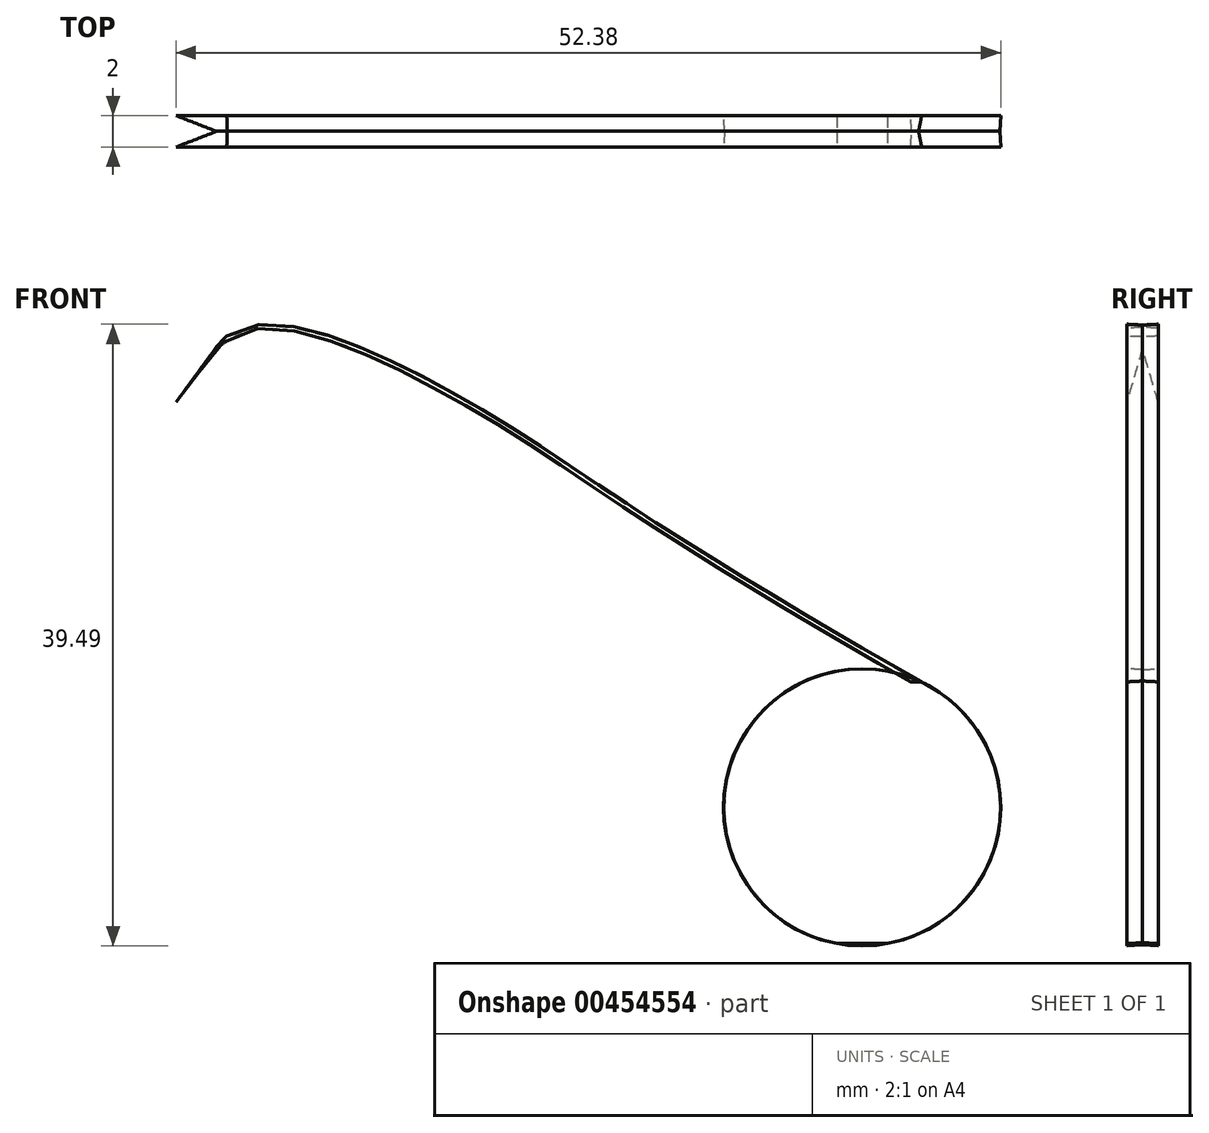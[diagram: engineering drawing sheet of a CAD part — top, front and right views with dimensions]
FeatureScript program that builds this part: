
annotation { "Feature Type Name" : "Feature", "Feature Type Description" : "" }
export const myFeature = defineFeature(function(context is Context, id is Id, definition is map)
    precondition{}
    {
        {
            var Q0;
            Q0=qCreatedBy(makeId("Front.planeOp"),FACE);
            var sketch = newSketch(context, id + "F0", { "sketchPlane" : qUnion([Q0])});
            skCircle(sketch, "E0", {"center": v(-75.56, 14) * mm, "radius": 2 * mm});
            skCircle(sketch, "E1", {"center": v(69.2, 8.6) * mm, "radius": 8.75 * mm});
            skLineSegment(sketch, "E2", {"start": v(-75.56, 14) * mm, "end": v(-75.56, -5.67) * mm});
            skLineSegment(sketch, "E3", {"start": v(-75.56, -5.67) * mm, "end": v(-75.56, 4.17) * mm, "construction": true});
            skSolve(sketch);
        }
        {
            var Q0;
            Q0=makeQuery(id+"F0.imprint","IMPRINT",FACE,{"disambiguationData":[TD([[makeQuery(id+"F0.imprint","IMPRINT",EDGE,{"derivedFrom":sQuery(id+"F0.wireOp",EDGE,"E1")}),1.0]])]});
            var sketch = newSketch(context, id + "F1", { "sketchPlane" : qUnion([Q0])});
            skLineSegment(sketch, "E4", {"start": v(-69.34, 0) * mm, "end": v(75.66, 0) * mm});
            skPoint(sketch, "E5", {"position": v(-60.14, 0) * mm});
            skPoint(sketch, "E6", {"position": v(-37.74, 0) * mm});
            skPoint(sketch, "E7", {"position": v(-0.84, 0) * mm});
            skPoint(sketch, "E8", {"position": v(24.04, 0) * mm});
            skPoint(sketch, "E9", {"position": v(29.16, 0) * mm});
            skPoint(sketch, "E10", {"position": v(-60.14, 6) * mm});
            skPoint(sketch, "E11", {"position": v(-0.84, 6.35) * mm});
            skPoint(sketch, "E12", {"position": v(24.04, 6) * mm});
            skPoint(sketch, "E13", {"position": v(-37.74, 16.6) * mm});
            skPoint(sketch, "E14", {"position": v(-55.56, 12) * mm});
            skPoint(sketch, "E15", {"position": v(-55.56, 0) * mm});
            skPoint(sketch, "E16", {"position": v(-0.84, 23.5) * mm});
            skPoint(sketch, "E17", {"position": v(23.36, 24) * mm});
            skPoint(sketch, "E18", {"position": v(29.16, 39.37) * mm});
            skLineSegment(sketch, "E19", {"start": v(75.66, 0) * mm, "end": v(75.66, 67.99) * mm, "construction": true});
            skSolve(sketch);
        }
        {
            var Q0;
            Q0=qCreatedBy(makeId("Front.planeOp"),FACE);
            var sketch = newSketch(context, id + "F2", { "sketchPlane" : qUnion([Q0])});
            skPoint(sketch, "E20.0.internal.orphan", {"position": v(-75.23, 15.99) * mm});
            skPoint(sketch, "E20.1.internal.orphan", {"position": v(-54.87, 12.03) * mm});
            skPoint(sketch, "E20.3.internal.orphan", {"position": v(0, 23) * mm});
            skFitSpline(sketch, "E21", {"points": [v(-75.23, 15.99) * mm, v(-54.87, 12.03) * mm, v(-36.58, 15.99) * mm, v(2, 23) * mm, v(24.58, 23) * mm, v(28.92, 38.53) * mm, v(45.28, 36.42) * mm, v(50.62, 33.94) * mm, v(76.35, 18.3) * mm, v(68.68, 17.05) * mm], "startDerivative": vector(159.5, -48.83) * mm, "endDerivative": vector(-180.17, 33.32) * mm});
            skFitSpline(sketch, "E22", {"points": [v(82.95, 8.08) * mm, v(82.95, 7.84) * mm], "startDerivative": vector(0, -0.24) * mm, "endDerivative": vector(0, -0.24) * mm});
            skPoint(sketch, "E23.2.internal.orphan", {"position": v(-42.24, 0) * mm});
            skPoint(sketch, "E23.4.internal.orphan", {"position": v(67.75, 0) * mm});
            skPoint(sketch, "E23.5.internal.orphan", {"position": v(67.62, 0) * mm});
            skPoint(sketch, "E23.start.orphan", {"position": v(-75.23, 12.03) * mm});
            skFitSpline(sketch, "E24", {"points": [v(-75.23, 15.99) * mm, v(-75.23, 12.03) * mm, v(0, 6.52) * mm, v(24.5, 5.95) * mm, v(38.8, 3.52) * mm, v(67.75, 0) * mm, v(76.63, 4.25) * mm, v(76.91, 12.03) * mm, v(73.01, 16.24) * mm], "startDerivative": vector(-33.24, -64.2) * mm, "endDerivative": vector(-53.14, 45.89) * mm});
            skFitSpline(sketch, "E25", {"points": [v(-54.94, 11.84) * mm, v(-36.69, 15.87) * mm, v(1.9, 22.9) * mm, v(24.48, 22.8) * mm, v(28.8, 38.37) * mm, v(44.2, 34.06) * mm, v(49.3, 30.9) * mm, v(73.01, 16.24) * mm], "startDerivative": vector(99.17, 21) * mm, "endDerivative": vector(225.76, -126.6) * mm});
            skFitSpline(sketch, "E26", {"points": [v(-54.88, 12.04) * mm, v(-36.58, 15.96) * mm, v(2, 22.96) * mm, v(24.58, 23.01) * mm, v(28.92, 38.52) * mm, v(44.31, 34.23) * mm, v(49.38, 31.09) * mm, v(73.48, 16.23) * mm], "startDerivative": vector(99.17, 21.02) * mm, "endDerivative": vector(225.75, -126.6) * mm});
            skFitSpline(sketch, "E27", {"points": [v(-54.88, 12.04) * mm, v(-36.58, 15.96) * mm, v(2, 22.96) * mm, v(24.58, 23.01) * mm, v(28.92, 38.52) * mm, v(44.31, 34.23) * mm, v(49.38, 31.09) * mm, v(73.48, 16.23) * mm], "startDerivative": vector(99.17, 21.02) * mm, "endDerivative": vector(225.75, -126.6) * mm});
            skSolve(sketch);
        }
        {
            var Q0;
            Q0=makeQuery(id+"F2.imprint","IMPRINT",FACE,{"disambiguationData":[TD([[makeQuery(id+"F2.imprint","IMPRINT",EDGE,{"derivedFrom":sQuery(id+"F2.wireOp",EDGE,"E21")}),-1.0]])]});
            var Q1;
            Q1=makeQuery(id+"F0.imprint","IMPRINT",FACE,{"disambiguationData":[TD([[makeQuery(id+"F0.imprint","IMPRINT",EDGE,{"derivedFrom":sQuery(id+"F0.wireOp",EDGE,"E1")}),1.0]])]});
            var Q2;
            {var subQ0=sQuery(id+"F1.wireOp",EDGE,"E4");var subQ1=makeQuery(id+"F0.imprint","IMPRINT",EDGE,{"derivedFrom":sQuery(id+"F0.wireOp",EDGE,"E1")});var subQ2=makeQuery(id+"F1.imprint","INTERSECT",VERTEX,{"disambiguationData":[OD(0.0)],"derivedFrom":[subQ1,subQ0]});Q2=makeQuery(id+"F1.imprint","IMPRINT",FACE,{"disambiguationData":[TD([[makeQuery(id+"F1.imprint","IMPRINT",EDGE,{"disambiguationData":[TD([[subQ2,-1.0]])],"derivedFrom":subQ0}),1.0]])]});}
            extrude(context, id + "F3", {"entities" : qUnion([Q0, Q1, Q2]), "endBound" : BoundingType.SYMMETRIC, "oppositeDirection" : true, "depth" : 2 * mm, "hasDraft" : true, "draftAngle" : 3 * degree});
        }
    });
